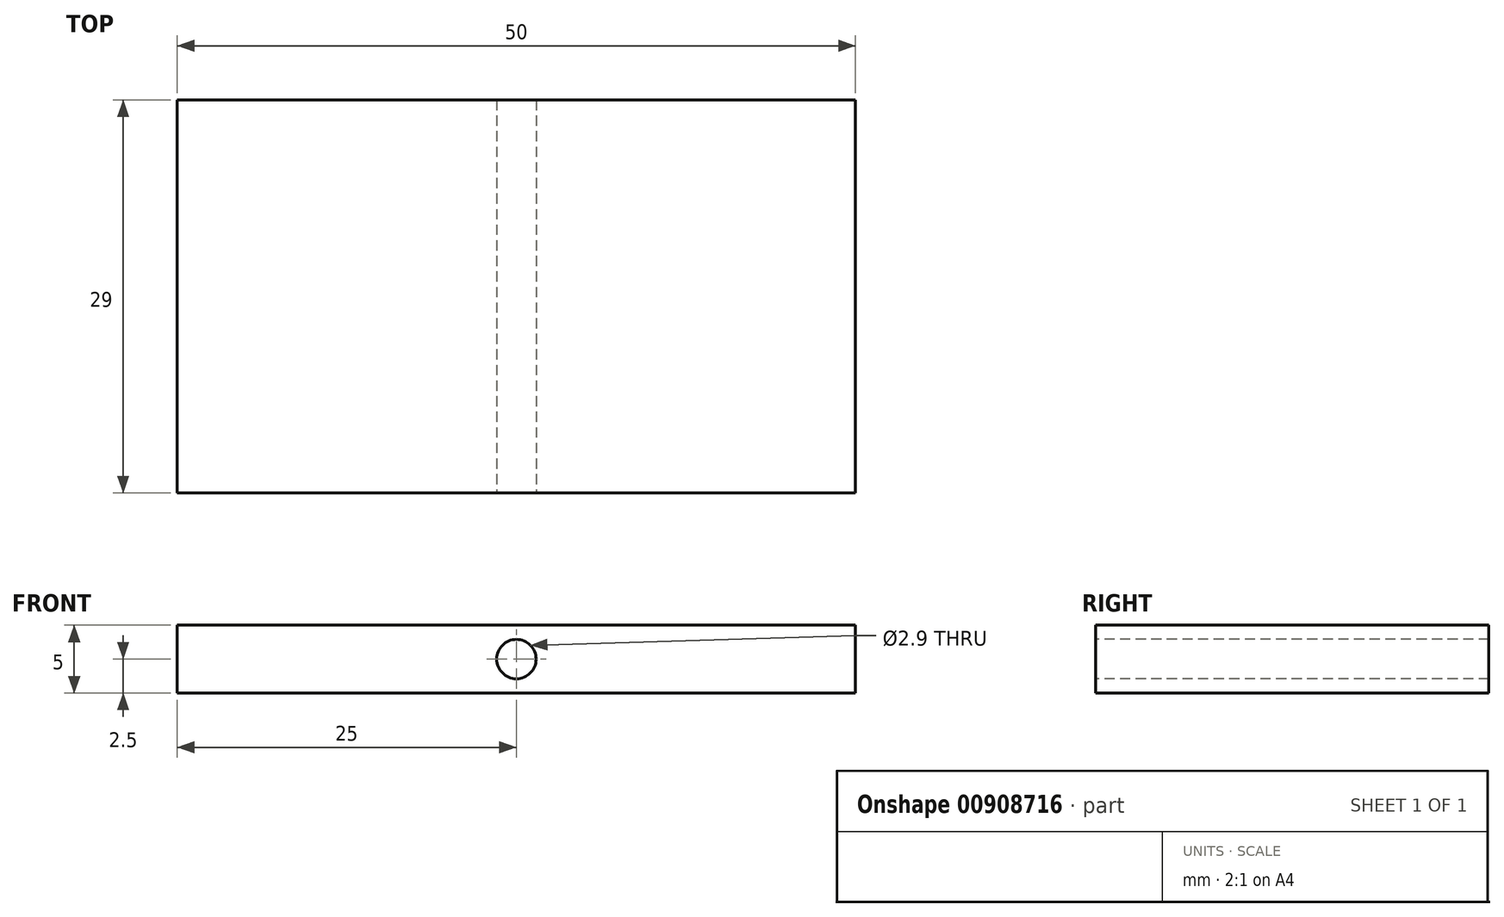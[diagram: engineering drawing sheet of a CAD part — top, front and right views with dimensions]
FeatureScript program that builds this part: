
annotation { "Feature Type Name" : "Feature", "Feature Type Description" : "" }
export const myFeature = defineFeature(function(context is Context, id is Id, definition is map)
    precondition{}
    {
        {
            var Q0;
            Q0=qCreatedBy(makeId("Top.planeOp"),FACE);
            var sketch = newSketch(context, id + "F0", { "sketchPlane" : qUnion([Q0])});
            skLineSegment(sketch, "E0.bottom", {"start": v(25, -14.5) * mm, "end": v(-25, -14.5) * mm});
            skLineSegment(sketch, "E0.top", {"start": v(25, 14.5) * mm, "end": v(-25, 14.5) * mm});
            skLineSegment(sketch, "E0.left", {"start": v(25, -14.5) * mm, "end": v(25, 14.5) * mm});
            skLineSegment(sketch, "E0.right", {"start": v(-25, -14.5) * mm, "end": v(-25, 14.5) * mm});
            skPoint(sketch, "E0.middle", {"position": v(0, 0) * mm});
            skSolve(sketch);
        }
        {
            var Q0;
            Q0=makeQuery(id+"F0.imprint","IMPRINT",FACE,{"disambiguationData":[TD([[makeQuery(id+"F0.imprint","IMPRINT",EDGE,{"derivedFrom":sQuery(id+"F0.wireOp",EDGE,"E0.bottom")}),-1.0]])]});
            extrude(context, id + "F1", {"entities" : qUnion([Q0]), "depth" : 5 * mm, "offsetDistance" : 25 * mm});
        }
        {
            var Q0;
            Q0=makeQuery(id+"F1.opExtrude","SWEPT_FACE",FACE,{"disambiguationData":[OSD([sQuery(id+"F0.wireOp",EDGE,"E0.bottom")])]});
            var sketch = newSketch(context, id + "F2", { "sketchPlane" : qUnion([Q0])});
            skCircle(sketch, "E1", {"center": v(0, 2.5) * mm, "radius": 1.45 * mm});
            skSolve(sketch);
        }
        {
            var Q0;
            Q0=makeQuery(id+"F2.imprint","IMPRINT",FACE,{"disambiguationData":[TD([[makeQuery(id+"F2.imprint","IMPRINT",EDGE,{"derivedFrom":sQuery(id+"F2.wireOp",EDGE,"E1")}),1.0]])]});
            extrude(context, id + "F3", {"entities" : qUnion([Q0]), "operationType" : NewBodyOperationType.REMOVE, "oppositeDirection" : true, "depth" : 38.6 * mm, "offsetDistance" : 25 * mm});
        }
    });
